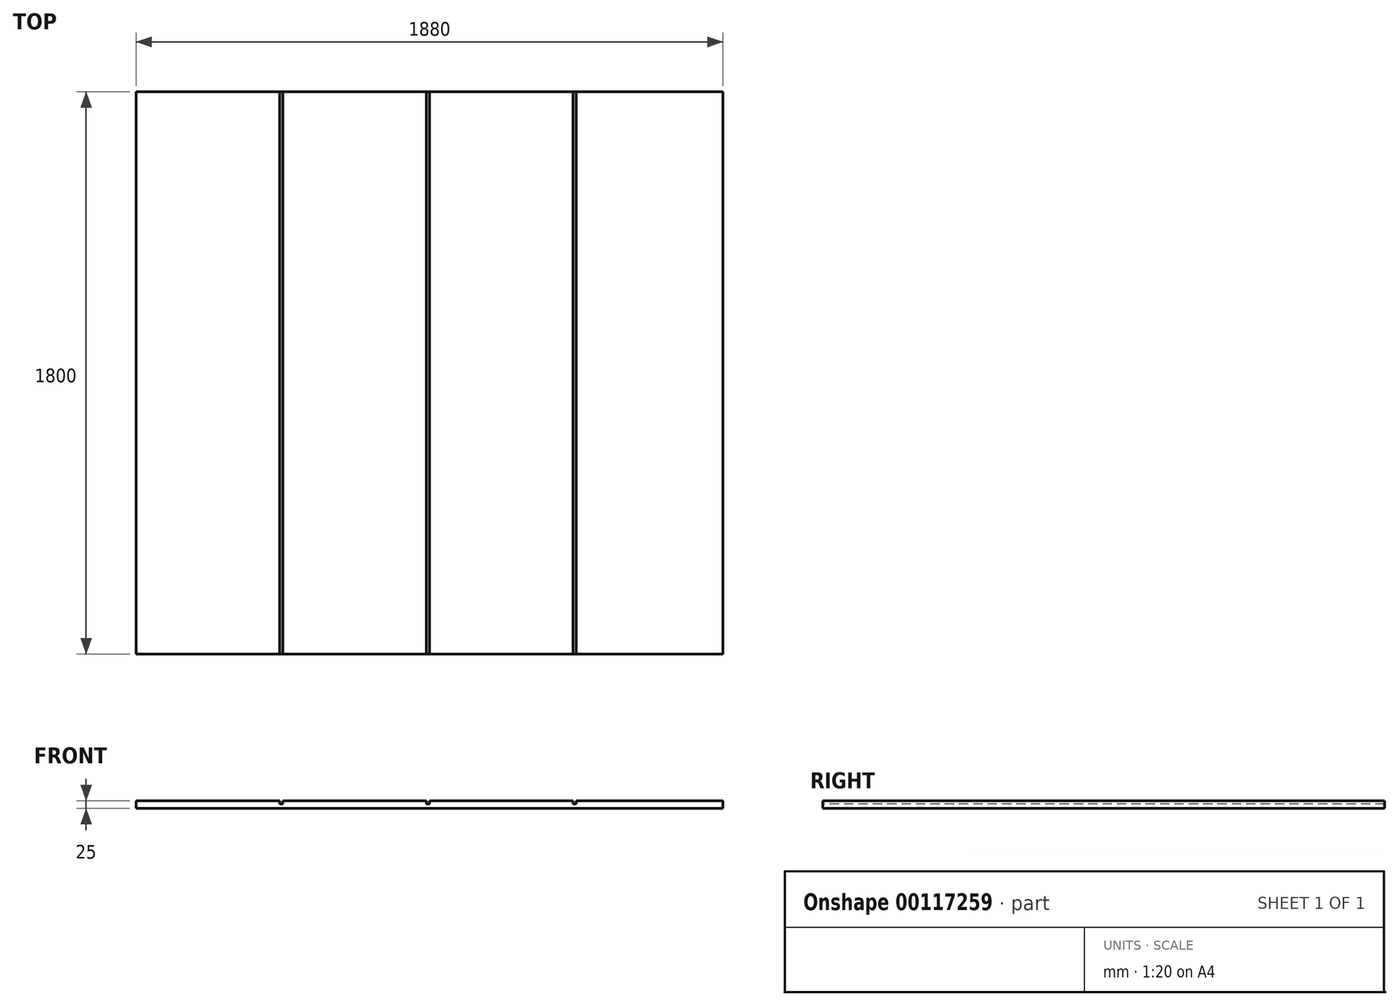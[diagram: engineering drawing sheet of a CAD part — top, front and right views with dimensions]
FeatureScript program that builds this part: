
annotation { "Feature Type Name" : "Feature", "Feature Type Description" : "" }
export const myFeature = defineFeature(function(context is Context, id is Id, definition is map)
    precondition{}
    {
        {
            var Q0;
            Q0=qCreatedBy(makeId("Top.planeOp"),FACE);
            var sketch = newSketch(context, id + "F0", { "sketchPlane" : qUnion([Q0])});
            skLineSegment(sketch, "E0.bottom", {"start": v(-29.17, 1756.6) * mm, "end": v(1850.83, 1756.6) * mm});
            skLineSegment(sketch, "E0.top", {"start": v(-29.17, -43.4) * mm, "end": v(1850.83, -43.4) * mm});
            skLineSegment(sketch, "E0.left", {"start": v(-29.17, 1756.6) * mm, "end": v(-29.17, -43.4) * mm});
            skLineSegment(sketch, "E0.right", {"start": v(1850.83, 1756.6) * mm, "end": v(1850.83, -43.4) * mm});
            skSolve(sketch);
        }
        {
            var Q0;
            Q0=makeQuery(id+"F0.imprint","IMPRINT",FACE,{"disambiguationData":[TD([[makeQuery(id+"F0.imprint","IMPRINT",EDGE,{"derivedFrom":sQuery(id+"F0.wireOp",EDGE,"E0.bottom")}),-1.0]])]});
            extrude(context, id + "F1", {"entities" : qUnion([Q0]), "depth" : 25 * mm});
        }
        {
            var Q0;
            Q0=makeQuery(id+"F1.opExtrude","CAP_FACE",FACE,{"disambiguationData":[OSD([sQuery(id+"F0.wireOp",EDGE,"E0.bottom"),sQuery(id+"F0.wireOp",EDGE,"E0.top"),sQuery(id+"F0.wireOp",EDGE,"E0.left"),sQuery(id+"F0.wireOp",EDGE,"E0.right")])],"isStart":false});
            var sketch = newSketch(context, id + "F2", { "sketchPlane" : qUnion([Q0])});
            skLineSegment(sketch, "E1.bottom", {"start": v(430.83, 1756.6) * mm, "end": v(440.83, 1756.6) * mm});
            skLineSegment(sketch, "E1.top", {"start": v(430.83, -43.4) * mm, "end": v(440.83, -43.4) * mm});
            skLineSegment(sketch, "E1.left", {"start": v(430.83, 1756.6) * mm, "end": v(430.83, -43.4) * mm});
            skLineSegment(sketch, "E1.right", {"start": v(440.83, 1756.6) * mm, "end": v(440.83, -43.4) * mm});
            skLineSegment(sketch, "E2.bottom", {"start": v(900.83, 1756.6) * mm, "end": v(910.83, 1756.6) * mm});
            skLineSegment(sketch, "E2.top", {"start": v(900.83, -43.4) * mm, "end": v(910.83, -43.4) * mm});
            skLineSegment(sketch, "E2.left", {"start": v(900.83, 1756.6) * mm, "end": v(900.83, -43.4) * mm});
            skLineSegment(sketch, "E2.right", {"start": v(910.83, 1756.6) * mm, "end": v(910.83, -43.4) * mm});
            skLineSegment(sketch, "E3.bottom", {"start": v(1370.83, 1756.6) * mm, "end": v(1380.83, 1756.6) * mm});
            skLineSegment(sketch, "E3.top", {"start": v(1370.83, -43.4) * mm, "end": v(1380.83, -43.4) * mm});
            skLineSegment(sketch, "E3.left", {"start": v(1370.83, 1756.6) * mm, "end": v(1370.83, -43.4) * mm});
            skLineSegment(sketch, "E3.right", {"start": v(1380.83, 1756.6) * mm, "end": v(1380.83, -43.4) * mm});
            skSolve(sketch);
        }
        {
            var Q0;
            Q0=makeQuery(id+"F2.imprint","IMPRINT",FACE,{"disambiguationData":[TD([[makeQuery(id+"F2.imprint","IMPRINT",EDGE,{"derivedFrom":sQuery(id+"F2.wireOp",EDGE,"E1.bottom")}),-1.0]])]});
            var Q1;
            Q1=makeQuery(id+"F2.imprint","IMPRINT",FACE,{"disambiguationData":[TD([[makeQuery(id+"F2.imprint","IMPRINT",EDGE,{"derivedFrom":sQuery(id+"F2.wireOp",EDGE,"E2.bottom")}),-1.0]])]});
            var Q2;
            Q2=makeQuery(id+"F2.imprint","IMPRINT",FACE,{"disambiguationData":[TD([[makeQuery(id+"F2.imprint","IMPRINT",EDGE,{"derivedFrom":sQuery(id+"F2.wireOp",EDGE,"E3.bottom")}),-1.0]])]});
            extrude(context, id + "F3", {"entities" : qUnion([Q0, Q1, Q2]), "operationType" : NewBodyOperationType.REMOVE, "oppositeDirection" : true, "depth" : 10 * mm});
        }
    });
